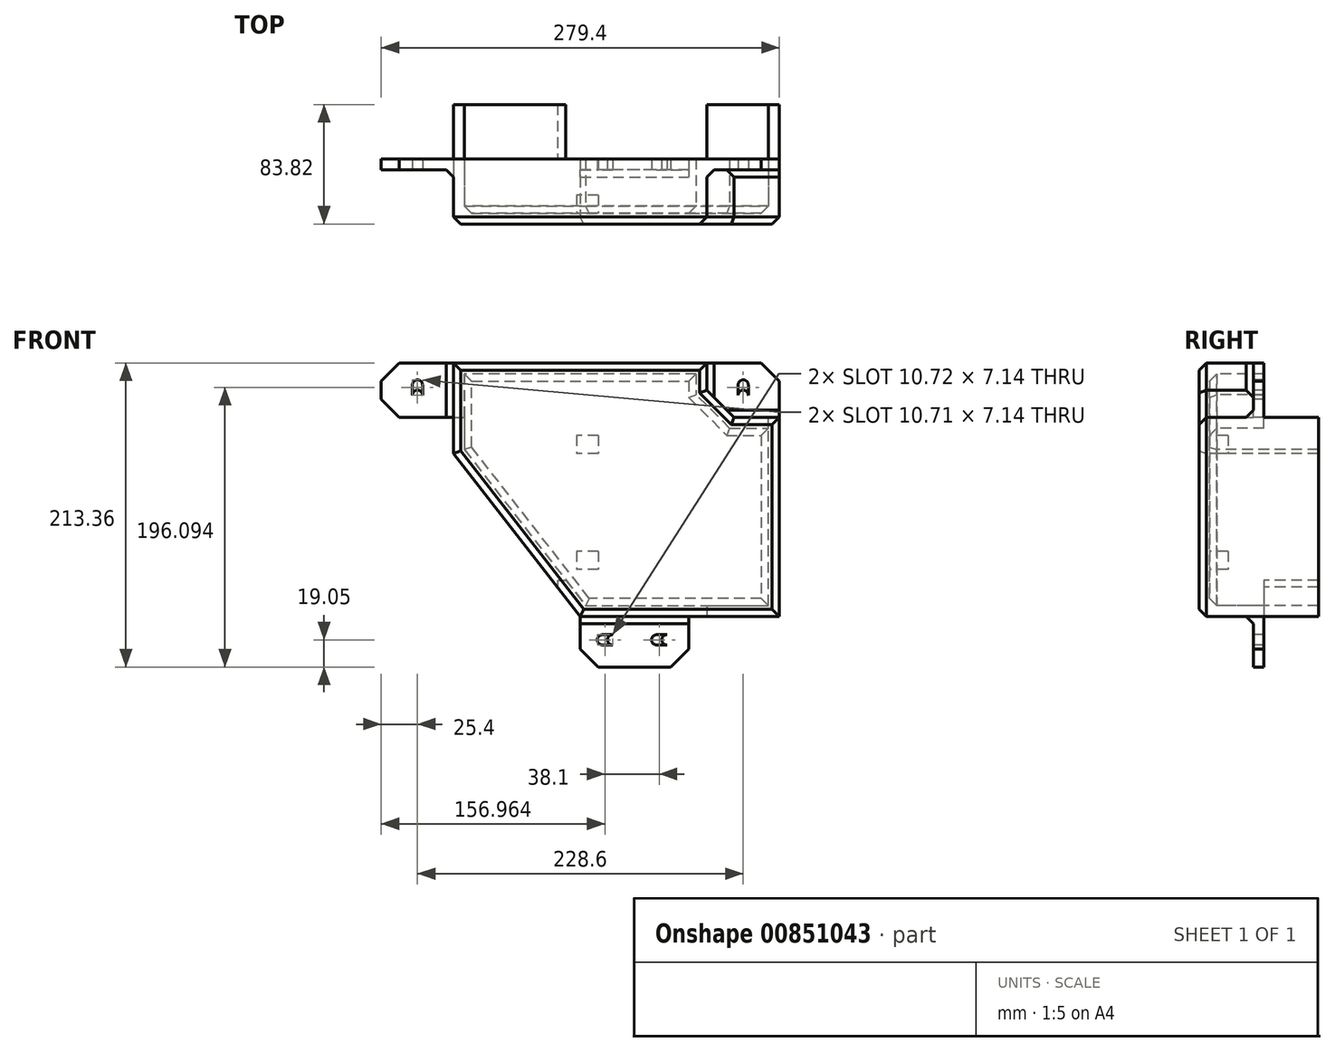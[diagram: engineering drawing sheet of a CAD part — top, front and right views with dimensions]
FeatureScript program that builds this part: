
annotation { "Feature Type Name" : "Feature", "Feature Type Description" : "" }
export const myFeature = defineFeature(function(context is Context, id is Id, definition is map)
    precondition{}
    {
        {
            var Q0;
            Q0=qCreatedBy(makeId("Front.planeOp"),FACE);
            var Q1;
            Q1=qCreatedBy(makeId("Front.planeOp"),FACE);
            var sketch = newSketch(context, id + "F0", { "sketchPlane" : qUnion([Q0, Q1])});
            skLineSegment(sketch, "E0.bottom", {"start": v(0, 0) * mm, "end": v(-279.4, 0) * mm});
            skLineSegment(sketch, "E0.top", {"start": v(0, 213.36) * mm, "end": v(-279.4, 213.36) * mm});
            skLineSegment(sketch, "E0.left", {"start": v(0, 0) * mm, "end": v(0, 213.36) * mm});
            skLineSegment(sketch, "E0.right", {"start": v(-279.4, 0) * mm, "end": v(-279.4, 213.36) * mm});
            skSolve(sketch);
        }
        {
            var Q0;
            Q0 = qSketchRegion(id + "F0", true);
            extrude(context, id + "F1", {"entities" : qUnion([Q0]), "depth" : 83.82 * mm, "offsetDistance" : 25.4 * mm});
        }
        {
            var Q0;
            Q0=makeQuery(id+"F1.opExtrude","CAP_FACE",FACE,{"disambiguationData":[OSD([sQuery(id+"F0.wireOp",EDGE,"E0.bottom"),sQuery(id+"F0.wireOp",EDGE,"E0.top"),sQuery(id+"F0.wireOp",EDGE,"E0.left"),sQuery(id+"F0.wireOp",EDGE,"E0.right")])],"isStart":false});
            var sketch = newSketch(context, id + "F2", { "sketchPlane" : qUnion([Q0])});
            skLineSegment(sketch, "E1.bottom", {"start": v(-50.8, 213.36) * mm, "end": v(0, 213.36) * mm});
            skLineSegment(sketch, "E1.top", {"start": v(-50.8, 175.26) * mm, "end": v(0, 175.26) * mm});
            skLineSegment(sketch, "E1.left", {"start": v(-50.8, 213.36) * mm, "end": v(-50.8, 175.26) * mm});
            skLineSegment(sketch, "E1.right", {"start": v(0, 213.36) * mm, "end": v(0, 175.26) * mm});
            skLineSegment(sketch, "E2", {"start": v(-228.6, 175.26) * mm, "end": v(-279.4, 175.26) * mm});
            skLineSegment(sketch, "E3", {"start": v(-228.6, 175.26) * mm, "end": v(-228.6, 213.36) * mm});
            skLineSegment(sketch, "E4", {"start": v(-228.6, 213.36) * mm, "end": v(-228.6, 149.86) * mm});
            skLineSegment(sketch, "E5", {"start": v(-228.6, 149.86) * mm, "end": v(-139.7, 35.56) * mm});
            skLineSegment(sketch, "E6", {"start": v(-139.7, 35.56) * mm, "end": v(0, 35.56) * mm});
            skLineSegment(sketch, "E7", {"start": v(-139.7, 35.56) * mm, "end": v(-139.7, 0) * mm});
            skLineSegment(sketch, "E8", {"start": v(-63.5, 35.56) * mm, "end": v(-63.5, 0) * mm});
            skLineSegment(sketch, "E9", {"start": v(-228.6, 175.26) * mm, "end": v(-50.8, 175.26) * mm});
            skLineSegment(sketch, "E10", {"start": v(-31.75, 175.26) * mm, "end": v(-50.8, 194.31) * mm});
            skSolve(sketch);
        }
        {
            var Q0;
            {var subQ1=sQuery(id+"F2.wireOp",EDGE,"E1.bottom");Q0=makeQuery(id+"F2.imprint","IMPRINT",FACE,{"disambiguationData":[TD([[makeQuery(id+"F2.imprint","IMPRINT",EDGE,{"derivedFrom":subQ1}),1.0]])]});}
            var Q1;
            {var subQ0=sQuery(id+"F2.wireOp",EDGE,"E7");Q1=makeQuery(id+"F2.imprint","IMPRINT",FACE,{"disambiguationData":[TD([[makeQuery(id+"F2.imprint","IMPRINT",EDGE,{"derivedFrom":subQ0}),1.0]])]});}
            var Q2;
            {var subQ0=sQuery(id+"F2.wireOp",EDGE,"E2");Q2=makeQuery(id+"F2.imprint","IMPRINT",FACE,{"disambiguationData":[TD([[makeQuery(id+"F2.imprint","IMPRINT",EDGE,{"derivedFrom":subQ0}),-1.0]])]});}
            var Q3;
            Q3=sQuery(id+"F2.wireOp",EDGE,"E2");
            var Q4;
            Q4=sQuery(id+"F2.wireOp",EDGE,"E3");
            var Q5;
            Q5=sQuery(id+"F2.wireOp",EDGE,"E1.left");
            var Q6;
            Q6=sQuery(id+"F2.wireOp",EDGE,"E1.top");
            var Q7;
            Q7=sQuery(id+"F2.wireOp",EDGE,"E6");
            var Q8;
            Q8=sQuery(id+"F2.wireOp",EDGE,"E7");
            extrude(context, id + "F3", {"entities" : qUnion([Q0, Q1, Q2]), "operationType" : NewBodyOperationType.REMOVE, "surfaceEntities" : qUnion([Q3, Q4, Q5, Q6, Q7, Q8]), "oppositeDirection" : true, "depth" : 38.1 * mm, "offsetDistance" : 25.4 * mm});
        }
        {
            var Q0;
            {var subQ4=sQuery(id+"F2.wireOp",EDGE,"E2");Q0=makeQuery(id+"F2.imprint","IMPRINT",FACE,{"disambiguationData":[TD([[makeQuery(id+"F2.imprint","IMPRINT",EDGE,{"derivedFrom":subQ4}),1.0]])]});}
            var Q1;
            {var subQ3=sQuery(id+"F2.wireOp",EDGE,"E8");Q1=makeQuery(id+"F2.imprint","IMPRINT",FACE,{"disambiguationData":[TD([[makeQuery(id+"F2.imprint","IMPRINT",EDGE,{"derivedFrom":subQ3}),1.0]])]});}
            extrude(context, id + "F4", {"entities" : qUnion([Q0, Q1]), "operationType" : NewBodyOperationType.REMOVE, "oppositeDirection" : true, "depth" : 83.82 * mm, "offsetDistance" : 25.4 * mm});
        }
        {
            var Q0;
            Q0=makeQuery(id+"F1.opExtrude","CAP_FACE",FACE,{"disambiguationData":[OSD([sQuery(id+"F0.wireOp",EDGE,"E0.bottom"),sQuery(id+"F0.wireOp",EDGE,"E0.top"),sQuery(id+"F0.wireOp",EDGE,"E0.left"),sQuery(id+"F0.wireOp",EDGE,"E0.right")])],"isStart":true});
            shell(context, id + "F5", {"entities" : qUnion([Q0]), "thickness" : 7.62 * mm});
        }
        {
            var Q0;
            Q0=makeQuery(id+"F1.opExtrude","SWEPT_FACE",FACE,{"disambiguationData":[OSD([sQuery(id+"F0.wireOp",EDGE,"E0.left")])]});
            var sketch = newSketch(context, id + "F6", { "sketchPlane" : qUnion([Q0])});
            skLineSegment(sketch, "E11.bottom", {"start": v(0, 213.36) * mm, "end": v(-38.1, 213.36) * mm});
            skLineSegment(sketch, "E11.top", {"start": v(0, 175.26) * mm, "end": v(-38.1, 175.26) * mm});
            skLineSegment(sketch, "E11.left", {"start": v(0, 213.36) * mm, "end": v(0, 175.26) * mm});
            skLineSegment(sketch, "E11.right", {"start": v(-38.1, 213.36) * mm, "end": v(-38.1, 175.26) * mm});
            skLineSegment(sketch, "E12.bottom", {"start": v(0, 0) * mm, "end": v(-38.1, 0) * mm});
            skLineSegment(sketch, "E12.top", {"start": v(0, 35.56) * mm, "end": v(-38.1, 35.56) * mm});
            skLineSegment(sketch, "E12.left", {"start": v(0, 0) * mm, "end": v(0, 35.56) * mm});
            skLineSegment(sketch, "E12.right", {"start": v(-38.1, 0) * mm, "end": v(-38.1, 35.56) * mm});
            skSolve(sketch);
        }
        {
            var Q0;
            Q0 = qSketchRegion(id + "F6", true);
            extrude(context, id + "F7", {"entities" : qUnion([Q0]), "operationType" : NewBodyOperationType.REMOVE, "oppositeDirection" : true, "depth" : 341.88 * mm, "offsetDistance" : 25.4 * mm});
        }
        {
            var Q0;
            Q0=makeQuery(id+"F3.boolean.opBoolean","COPY",FACE,{"derivedFrom":makeQuery(id+"F3.opExtrude","CAP_FACE",FACE,{"disambiguationData":[OSD([sQuery(id+"F0.wireOp",EDGE,"E0.bottom"),sQuery(id+"F2.wireOp",EDGE,"E6"),sQuery(id+"F2.wireOp",EDGE,"E7"),sQuery(id+"F2.wireOp",EDGE,"E8")])],"isStart":false})});
            var sketch = newSketch(context, id + "F8", { "sketchPlane" : qUnion([Q0])});
            skCircle(sketch, "E13", {"center": v(-82.55, 19.05) * mm, "radius": 3.57 * mm});
            skCircle(sketch, "E14", {"center": v(-120.65, 19.05) * mm, "radius": 3.57 * mm});
            skLineSegment(sketch, "E15", {"start": v(-139.7, 12.7) * mm, "end": v(-127, 0) * mm});
            skLineSegment(sketch, "E16", {"start": v(-76.2, 0) * mm, "end": v(-63.5, 12.7) * mm});
            skLineSegment(sketch, "E17", {"start": v(-139.7, 0) * mm, "end": v(-63.5, 0) * mm});
            skCircle(sketch, "E18", {"center": v(-254, 194.3) * mm, "radius": 3.57 * mm});
            skCircle(sketch, "E19", {"center": v(-25.4, 194.3) * mm, "radius": 3.57 * mm});
            skLineSegment(sketch, "E20.0.0", {"start": v(-228.6, 175.26) * mm, "end": v(-228.6, 213.36) * mm});
            skLineSegment(sketch, "E20.0.1", {"start": v(-228.6, 213.36) * mm, "end": v(-279.4, 213.36) * mm});
            skLineSegment(sketch, "E20.0.2", {"start": v(-279.4, 213.36) * mm, "end": v(-279.4, 175.26) * mm});
            skLineSegment(sketch, "E20.0.3", {"start": v(-279.4, 175.26) * mm, "end": v(-228.6, 175.26) * mm});
            skLineSegment(sketch, "E21.0.0", {"start": v(0, 213.36) * mm, "end": v(-50.8, 213.36) * mm});
            skLineSegment(sketch, "E21.0.1", {"start": v(-50.8, 213.36) * mm, "end": v(-50.8, 194.31) * mm});
            skLineSegment(sketch, "E21.0.3", {"start": v(0, 175.26) * mm, "end": v(0, 213.36) * mm});
            skLineSegment(sketch, "E22", {"start": v(-266.7, 175.26) * mm, "end": v(-279.4, 187.96) * mm});
            skLineSegment(sketch, "E23", {"start": v(-266.7, 213.36) * mm, "end": v(-279.4, 200.66) * mm});
            skLineSegment(sketch, "E24", {"start": v(-12.7, 213.36) * mm, "end": v(0, 200.66) * mm});
            skCircle(sketch, "E25", {"center": v(-25.4, 197.88) * mm, "radius": 3.57 * mm});
            skCircle(sketch, "E26", {"center": v(-25.4, 190.74) * mm, "radius": 3.57 * mm});
            skLineSegment(sketch, "E27", {"start": v(-21.83, 197.88) * mm, "end": v(-21.83, 190.74) * mm});
            skLineSegment(sketch, "E28", {"start": v(-28.97, 197.88) * mm, "end": v(-28.97, 190.74) * mm});
            skCircle(sketch, "E29", {"center": v(-254, 197.88) * mm, "radius": 3.57 * mm});
            skCircle(sketch, "E30", {"center": v(-254, 190.74) * mm, "radius": 3.57 * mm});
            skLineSegment(sketch, "E31", {"start": v(-257.57, 197.88) * mm, "end": v(-257.57, 190.74) * mm});
            skLineSegment(sketch, "E32", {"start": v(-250.43, 197.88) * mm, "end": v(-250.43, 190.74) * mm});
            skCircle(sketch, "E33", {"center": v(-86.12, 19.05) * mm, "radius": 3.57 * mm});
            skCircle(sketch, "E34", {"center": v(-78.98, 19.05) * mm, "radius": 3.57 * mm});
            skLineSegment(sketch, "E35", {"start": v(-86.12, 22.62) * mm, "end": v(-78.98, 22.62) * mm});
            skLineSegment(sketch, "E36", {"start": v(-78.98, 15.48) * mm, "end": v(-86.12, 15.48) * mm});
            skCircle(sketch, "E37", {"center": v(-117.08, 19.05) * mm, "radius": 3.57 * mm});
            skCircle(sketch, "E38", {"center": v(-124.22, 19.05) * mm, "radius": 3.57 * mm});
            skLineSegment(sketch, "E39", {"start": v(-124.22, 22.62) * mm, "end": v(-117.08, 22.62) * mm});
            skLineSegment(sketch, "E40", {"start": v(-117.08, 15.48) * mm, "end": v(-124.22, 15.48) * mm});
            skSolve(sketch);
        }
        {
            var Q0;
            Q0=makeQuery(id+"F8.imprint","IMPRINT",FACE,{"disambiguationData":[TD([[makeQuery(id+"F8.imprint","IMPRINT",EDGE,{"derivedFrom":sQuery(id+"F8.wireOp",EDGE,"E19")}),1.0]])]});
            var Q1;
            {var subQ3=sQuery(id+"F8.wireOp",EDGE,"E24");Q1=makeQuery(id+"F8.imprint","IMPRINT",FACE,{"disambiguationData":[TD([[makeQuery(id+"F8.imprint","IMPRINT",EDGE,{"derivedFrom":subQ3}),1.0]])]});}
            var Q2;
            Q2=makeQuery(id+"F8.imprint","IMPRINT",FACE,{"disambiguationData":[TD([[makeQuery(id+"F8.imprint","IMPRINT",EDGE,{"derivedFrom":sQuery(id+"F8.wireOp",EDGE,"E18")}),1.0]])]});
            var Q3;
            {var subQ3=sQuery(id+"F8.wireOp",EDGE,"E23");Q3=makeQuery(id+"F8.imprint","IMPRINT",FACE,{"disambiguationData":[TD([[makeQuery(id+"F8.imprint","IMPRINT",EDGE,{"derivedFrom":subQ3}),-1.0]])]});}
            var Q4;
            {var subQ3=sQuery(id+"F8.wireOp",EDGE,"E22");Q4=makeQuery(id+"F8.imprint","IMPRINT",FACE,{"disambiguationData":[TD([[makeQuery(id+"F8.imprint","IMPRINT",EDGE,{"derivedFrom":subQ3}),1.0]])]});}
            var Q5;
            {var subQ0=sQuery(id+"F8.wireOp",EDGE,"E15");Q5=makeQuery(id+"F8.imprint","IMPRINT",FACE,{"disambiguationData":[TD([[makeQuery(id+"F8.imprint","IMPRINT",EDGE,{"derivedFrom":subQ0}),-1.0]])]});}
            var Q6;
            {var subQ0=sQuery(id+"F8.wireOp",EDGE,"E16");Q6=makeQuery(id+"F8.imprint","IMPRINT",FACE,{"disambiguationData":[TD([[makeQuery(id+"F8.imprint","IMPRINT",EDGE,{"derivedFrom":subQ0}),-1.0]])]});}
            var Q7;
            Q7=makeQuery(id+"F8.imprint","IMPRINT",FACE,{"disambiguationData":[TD([[makeQuery(id+"F8.imprint","IMPRINT",EDGE,{"derivedFrom":sQuery(id+"F8.wireOp",EDGE,"E13")}),1.0]])]});
            var Q8;
            Q8=makeQuery(id+"F8.imprint","IMPRINT",FACE,{"disambiguationData":[TD([[makeQuery(id+"F8.imprint","IMPRINT",EDGE,{"derivedFrom":sQuery(id+"F8.wireOp",EDGE,"E14")}),1.0]])]});
            var Q9;
            {var subQ0=sQuery(id+"F8.wireOp",EDGE,"E25");var subQ1=sQuery(id+"F8.wireOp",EDGE,"E19");var subQ2=makeQuery(id+"F8.imprint","INTERSECT",VERTEX,{"disambiguationData":[OD(0.0)],"derivedFrom":[subQ1,subQ0]});Q9=makeQuery(id+"F8.imprint","IMPRINT",FACE,{"disambiguationData":[TD([[makeQuery(id+"F8.imprint","IMPRINT",EDGE,{"disambiguationData":[TD([[subQ2,-1.0]])],"derivedFrom":subQ1}),-1.0]])]});}
            var Q10;
            {var subQ0=sQuery(id+"F8.wireOp",EDGE,"E25");var subQ1=sQuery(id+"F8.wireOp",EDGE,"E19");var subQ2=makeQuery(id+"F8.imprint","INTERSECT",VERTEX,{"disambiguationData":[OD(0.0)],"derivedFrom":[subQ1,subQ0]});Q10=makeQuery(id+"F8.imprint","IMPRINT",FACE,{"disambiguationData":[TD([[makeQuery(id+"F8.imprint","IMPRINT",EDGE,{"disambiguationData":[TD([[subQ2,-1.0]])],"derivedFrom":subQ1}),1.0]])]});}
            var Q11;
            {var subQ0=sQuery(id+"F8.wireOp",EDGE,"E26");var subQ1=sQuery(id+"F8.wireOp",EDGE,"E19");var subQ2=makeQuery(id+"F8.imprint","INTERSECT",VERTEX,{"disambiguationData":[OD(0.0)],"derivedFrom":[subQ1,subQ0]});Q11=makeQuery(id+"F8.imprint","IMPRINT",FACE,{"disambiguationData":[TD([[makeQuery(id+"F8.imprint","IMPRINT",EDGE,{"disambiguationData":[TD([[subQ2,-1.0]])],"derivedFrom":subQ1}),1.0]])]});}
            var Q12;
            {var subQ0=sQuery(id+"F8.wireOp",EDGE,"E26");var subQ1=sQuery(id+"F8.wireOp",EDGE,"E19");var subQ2=makeQuery(id+"F8.imprint","INTERSECT",VERTEX,{"disambiguationData":[OD(0.0)],"derivedFrom":[subQ1,subQ0]});Q12=makeQuery(id+"F8.imprint","IMPRINT",FACE,{"disambiguationData":[TD([[makeQuery(id+"F8.imprint","IMPRINT",EDGE,{"disambiguationData":[TD([[subQ2,-1.0]])],"derivedFrom":subQ1}),-1.0]])]});}
            var Q13;
            {var subQ0=sQuery(id+"F8.wireOp",EDGE,"E28");var subQ1=sQuery(id+"F8.wireOp",EDGE,"E19");var subQ2=makeQuery(id+"F8.imprint","INTERSECT",VERTEX,{"derivedFrom":[subQ1,subQ0]});Q13=makeQuery(id+"F8.imprint","IMPRINT",FACE,{"disambiguationData":[TD([[makeQuery(id+"F8.imprint","IMPRINT",EDGE,{"disambiguationData":[TD([[subQ2,1.0]])],"derivedFrom":subQ1}),-1.0]])]});}
            var Q14;
            {var subQ0=sQuery(id+"F8.wireOp",EDGE,"E27");var subQ1=sQuery(id+"F8.wireOp",EDGE,"E19");var subQ2=makeQuery(id+"F8.imprint","INTERSECT",VERTEX,{"derivedFrom":[subQ1,subQ0]});Q14=makeQuery(id+"F8.imprint","IMPRINT",FACE,{"disambiguationData":[TD([[makeQuery(id+"F8.imprint","IMPRINT",EDGE,{"disambiguationData":[TD([[subQ2,-1.0]])],"derivedFrom":subQ1}),-1.0]])]});}
            var Q15;
            {var subQ0=sQuery(id+"F8.wireOp",EDGE,"E27");var subQ1=sQuery(id+"F8.wireOp",EDGE,"E19");var subQ2=makeQuery(id+"F8.imprint","INTERSECT",VERTEX,{"derivedFrom":[subQ1,subQ0]});Q15=makeQuery(id+"F8.imprint","IMPRINT",FACE,{"disambiguationData":[TD([[makeQuery(id+"F8.imprint","IMPRINT",EDGE,{"disambiguationData":[TD([[subQ2,1.0]])],"derivedFrom":subQ1}),-1.0]])]});}
            var Q16;
            {var subQ0=sQuery(id+"F8.wireOp",EDGE,"E28");var subQ1=sQuery(id+"F8.wireOp",EDGE,"E19");var subQ2=makeQuery(id+"F8.imprint","INTERSECT",VERTEX,{"derivedFrom":[subQ1,subQ0]});Q16=makeQuery(id+"F8.imprint","IMPRINT",FACE,{"disambiguationData":[TD([[makeQuery(id+"F8.imprint","IMPRINT",EDGE,{"disambiguationData":[TD([[subQ2,-1.0]])],"derivedFrom":subQ1}),-1.0]])]});}
            var Q17;
            {var subQ0=sQuery(id+"F8.wireOp",EDGE,"E38");var subQ1=sQuery(id+"F8.wireOp",EDGE,"E14");var subQ2=makeQuery(id+"F8.imprint","INTERSECT",VERTEX,{"disambiguationData":[OD(0.0)],"derivedFrom":[subQ1,subQ0]});Q17=makeQuery(id+"F8.imprint","IMPRINT",FACE,{"disambiguationData":[TD([[makeQuery(id+"F8.imprint","IMPRINT",EDGE,{"disambiguationData":[TD([[subQ2,-1.0]])],"derivedFrom":subQ1}),1.0]])]});}
            var Q18;
            {var subQ0=sQuery(id+"F8.wireOp",EDGE,"E37");var subQ1=sQuery(id+"F8.wireOp",EDGE,"E14");var subQ2=makeQuery(id+"F8.imprint","INTERSECT",VERTEX,{"disambiguationData":[OD(0.0)],"derivedFrom":[subQ1,subQ0]});Q18=makeQuery(id+"F8.imprint","IMPRINT",FACE,{"disambiguationData":[TD([[makeQuery(id+"F8.imprint","IMPRINT",EDGE,{"disambiguationData":[TD([[subQ2,1.0]])],"derivedFrom":subQ1}),1.0]])]});}
            var Q19;
            {var subQ0=sQuery(id+"F8.wireOp",EDGE,"E37");var subQ1=sQuery(id+"F8.wireOp",EDGE,"E14");var subQ2=makeQuery(id+"F8.imprint","INTERSECT",VERTEX,{"disambiguationData":[OD(0.0)],"derivedFrom":[subQ1,subQ0]});Q19=makeQuery(id+"F8.imprint","IMPRINT",FACE,{"disambiguationData":[TD([[makeQuery(id+"F8.imprint","IMPRINT",EDGE,{"disambiguationData":[TD([[subQ2,1.0]])],"derivedFrom":subQ1}),-1.0]])]});}
            var Q20;
            {var subQ0=sQuery(id+"F8.wireOp",EDGE,"E38");var subQ1=sQuery(id+"F8.wireOp",EDGE,"E14");var subQ2=makeQuery(id+"F8.imprint","INTERSECT",VERTEX,{"disambiguationData":[OD(0.0)],"derivedFrom":[subQ1,subQ0]});Q20=makeQuery(id+"F8.imprint","IMPRINT",FACE,{"disambiguationData":[TD([[makeQuery(id+"F8.imprint","IMPRINT",EDGE,{"disambiguationData":[TD([[subQ2,-1.0]])],"derivedFrom":subQ1}),-1.0]])]});}
            var Q21;
            {var subQ0=sQuery(id+"F8.wireOp",EDGE,"E39");var subQ1=sQuery(id+"F8.wireOp",EDGE,"E14");var subQ2=makeQuery(id+"F8.imprint","INTERSECT",VERTEX,{"derivedFrom":[subQ1,subQ0]});Q21=makeQuery(id+"F8.imprint","IMPRINT",FACE,{"disambiguationData":[TD([[makeQuery(id+"F8.imprint","IMPRINT",EDGE,{"disambiguationData":[TD([[subQ2,1.0]])],"derivedFrom":subQ1}),-1.0]])]});}
            var Q22;
            {var subQ0=sQuery(id+"F8.wireOp",EDGE,"E39");var subQ1=sQuery(id+"F8.wireOp",EDGE,"E14");var subQ2=makeQuery(id+"F8.imprint","INTERSECT",VERTEX,{"derivedFrom":[subQ1,subQ0]});Q22=makeQuery(id+"F8.imprint","IMPRINT",FACE,{"disambiguationData":[TD([[makeQuery(id+"F8.imprint","IMPRINT",EDGE,{"disambiguationData":[TD([[subQ2,-1.0]])],"derivedFrom":subQ1}),-1.0]])]});}
            var Q23;
            {var subQ0=sQuery(id+"F8.wireOp",EDGE,"E40");var subQ1=sQuery(id+"F8.wireOp",EDGE,"E14");var subQ2=makeQuery(id+"F8.imprint","INTERSECT",VERTEX,{"derivedFrom":[subQ1,subQ0]});Q23=makeQuery(id+"F8.imprint","IMPRINT",FACE,{"disambiguationData":[TD([[makeQuery(id+"F8.imprint","IMPRINT",EDGE,{"disambiguationData":[TD([[subQ2,-1.0]])],"derivedFrom":subQ1}),-1.0]])]});}
            var Q24;
            {var subQ0=sQuery(id+"F8.wireOp",EDGE,"E38");var subQ1=sQuery(id+"F8.wireOp",EDGE,"E14");var subQ2=makeQuery(id+"F8.imprint","INTERSECT",VERTEX,{"disambiguationData":[OD(1.0)],"derivedFrom":[subQ1,subQ0]});Q24=makeQuery(id+"F8.imprint","IMPRINT",FACE,{"disambiguationData":[TD([[makeQuery(id+"F8.imprint","IMPRINT",EDGE,{"disambiguationData":[TD([[subQ2,-1.0]])],"derivedFrom":subQ1}),-1.0]])]});}
            var Q25;
            {var subQ0=sQuery(id+"F8.wireOp",EDGE,"E35");var subQ1=sQuery(id+"F8.wireOp",EDGE,"E13");var subQ2=makeQuery(id+"F8.imprint","INTERSECT",VERTEX,{"derivedFrom":[subQ1,subQ0]});Q25=makeQuery(id+"F8.imprint","IMPRINT",FACE,{"disambiguationData":[TD([[makeQuery(id+"F8.imprint","IMPRINT",EDGE,{"disambiguationData":[TD([[subQ2,1.0]])],"derivedFrom":subQ1}),-1.0]])]});}
            var Q26;
            {var subQ0=sQuery(id+"F8.wireOp",EDGE,"E35");var subQ1=sQuery(id+"F8.wireOp",EDGE,"E13");var subQ2=makeQuery(id+"F8.imprint","INTERSECT",VERTEX,{"derivedFrom":[subQ1,subQ0]});Q26=makeQuery(id+"F8.imprint","IMPRINT",FACE,{"disambiguationData":[TD([[makeQuery(id+"F8.imprint","IMPRINT",EDGE,{"disambiguationData":[TD([[subQ2,-1.0]])],"derivedFrom":subQ1}),-1.0]])]});}
            var Q27;
            {var subQ0=sQuery(id+"F8.wireOp",EDGE,"E33");var subQ1=sQuery(id+"F8.wireOp",EDGE,"E13");var subQ2=makeQuery(id+"F8.imprint","INTERSECT",VERTEX,{"disambiguationData":[OD(0.0)],"derivedFrom":[subQ1,subQ0]});Q27=makeQuery(id+"F8.imprint","IMPRINT",FACE,{"disambiguationData":[TD([[makeQuery(id+"F8.imprint","IMPRINT",EDGE,{"disambiguationData":[TD([[subQ2,-1.0]])],"derivedFrom":subQ1}),-1.0]])]});}
            var Q28;
            {var subQ0=sQuery(id+"F8.wireOp",EDGE,"E33");var subQ1=sQuery(id+"F8.wireOp",EDGE,"E13");var subQ2=makeQuery(id+"F8.imprint","INTERSECT",VERTEX,{"disambiguationData":[OD(0.0)],"derivedFrom":[subQ1,subQ0]});Q28=makeQuery(id+"F8.imprint","IMPRINT",FACE,{"disambiguationData":[TD([[makeQuery(id+"F8.imprint","IMPRINT",EDGE,{"disambiguationData":[TD([[subQ2,-1.0]])],"derivedFrom":subQ1}),1.0]])]});}
            var Q29;
            {var subQ0=sQuery(id+"F8.wireOp",EDGE,"E34");var subQ1=sQuery(id+"F8.wireOp",EDGE,"E13");var subQ2=makeQuery(id+"F8.imprint","INTERSECT",VERTEX,{"disambiguationData":[OD(0.0)],"derivedFrom":[subQ1,subQ0]});Q29=makeQuery(id+"F8.imprint","IMPRINT",FACE,{"disambiguationData":[TD([[makeQuery(id+"F8.imprint","IMPRINT",EDGE,{"disambiguationData":[TD([[subQ2,1.0]])],"derivedFrom":subQ1}),1.0]])]});}
            var Q30;
            {var subQ0=sQuery(id+"F8.wireOp",EDGE,"E34");var subQ1=sQuery(id+"F8.wireOp",EDGE,"E13");var subQ2=makeQuery(id+"F8.imprint","INTERSECT",VERTEX,{"disambiguationData":[OD(0.0)],"derivedFrom":[subQ1,subQ0]});Q30=makeQuery(id+"F8.imprint","IMPRINT",FACE,{"disambiguationData":[TD([[makeQuery(id+"F8.imprint","IMPRINT",EDGE,{"disambiguationData":[TD([[subQ2,1.0]])],"derivedFrom":subQ1}),-1.0]])]});}
            var Q31;
            {var subQ0=sQuery(id+"F8.wireOp",EDGE,"E36");var subQ1=sQuery(id+"F8.wireOp",EDGE,"E13");var subQ2=makeQuery(id+"F8.imprint","INTERSECT",VERTEX,{"derivedFrom":[subQ1,subQ0]});Q31=makeQuery(id+"F8.imprint","IMPRINT",FACE,{"disambiguationData":[TD([[makeQuery(id+"F8.imprint","IMPRINT",EDGE,{"disambiguationData":[TD([[subQ2,-1.0]])],"derivedFrom":subQ1}),-1.0]])]});}
            var Q32;
            {var subQ0=sQuery(id+"F8.wireOp",EDGE,"E33");var subQ1=sQuery(id+"F8.wireOp",EDGE,"E13");var subQ2=makeQuery(id+"F8.imprint","INTERSECT",VERTEX,{"disambiguationData":[OD(1.0)],"derivedFrom":[subQ1,subQ0]});Q32=makeQuery(id+"F8.imprint","IMPRINT",FACE,{"disambiguationData":[TD([[makeQuery(id+"F8.imprint","IMPRINT",EDGE,{"disambiguationData":[TD([[subQ2,-1.0]])],"derivedFrom":subQ1}),-1.0]])]});}
            var Q33;
            {var subQ0=sQuery(id+"F8.wireOp",EDGE,"E29");var subQ1=sQuery(id+"F8.wireOp",EDGE,"E18");var subQ2=makeQuery(id+"F8.imprint","INTERSECT",VERTEX,{"disambiguationData":[OD(0.0)],"derivedFrom":[subQ1,subQ0]});Q33=makeQuery(id+"F8.imprint","IMPRINT",FACE,{"disambiguationData":[TD([[makeQuery(id+"F8.imprint","IMPRINT",EDGE,{"disambiguationData":[TD([[subQ2,-1.0]])],"derivedFrom":subQ1}),1.0]])]});}
            var Q34;
            {var subQ0=sQuery(id+"F8.wireOp",EDGE,"E29");var subQ1=sQuery(id+"F8.wireOp",EDGE,"E18");var subQ2=makeQuery(id+"F8.imprint","INTERSECT",VERTEX,{"disambiguationData":[OD(0.0)],"derivedFrom":[subQ1,subQ0]});Q34=makeQuery(id+"F8.imprint","IMPRINT",FACE,{"disambiguationData":[TD([[makeQuery(id+"F8.imprint","IMPRINT",EDGE,{"disambiguationData":[TD([[subQ2,-1.0]])],"derivedFrom":subQ1}),-1.0]])]});}
            var Q35;
            {var subQ0=sQuery(id+"F8.wireOp",EDGE,"E30");var subQ1=sQuery(id+"F8.wireOp",EDGE,"E18");var subQ2=makeQuery(id+"F8.imprint","INTERSECT",VERTEX,{"disambiguationData":[OD(0.0)],"derivedFrom":[subQ1,subQ0]});Q35=makeQuery(id+"F8.imprint","IMPRINT",FACE,{"disambiguationData":[TD([[makeQuery(id+"F8.imprint","IMPRINT",EDGE,{"disambiguationData":[TD([[subQ2,-1.0]])],"derivedFrom":subQ1}),1.0]])]});}
            var Q36;
            {var subQ0=sQuery(id+"F8.wireOp",EDGE,"E30");var subQ1=sQuery(id+"F8.wireOp",EDGE,"E18");var subQ2=makeQuery(id+"F8.imprint","INTERSECT",VERTEX,{"disambiguationData":[OD(0.0)],"derivedFrom":[subQ1,subQ0]});Q36=makeQuery(id+"F8.imprint","IMPRINT",FACE,{"disambiguationData":[TD([[makeQuery(id+"F8.imprint","IMPRINT",EDGE,{"disambiguationData":[TD([[subQ2,-1.0]])],"derivedFrom":subQ1}),-1.0]])]});}
            var Q37;
            {var subQ0=sQuery(id+"F8.wireOp",EDGE,"E32");var subQ1=sQuery(id+"F8.wireOp",EDGE,"E18");var subQ2=makeQuery(id+"F8.imprint","INTERSECT",VERTEX,{"derivedFrom":[subQ1,subQ0]});Q37=makeQuery(id+"F8.imprint","IMPRINT",FACE,{"disambiguationData":[TD([[makeQuery(id+"F8.imprint","IMPRINT",EDGE,{"disambiguationData":[TD([[subQ2,1.0]])],"derivedFrom":subQ1}),-1.0]])]});}
            var Q38;
            {var subQ0=sQuery(id+"F8.wireOp",EDGE,"E29");var subQ1=sQuery(id+"F8.wireOp",EDGE,"E18");var subQ2=makeQuery(id+"F8.imprint","INTERSECT",VERTEX,{"disambiguationData":[OD(0.0)],"derivedFrom":[subQ1,subQ0]});Q38=makeQuery(id+"F8.imprint","IMPRINT",FACE,{"disambiguationData":[TD([[makeQuery(id+"F8.imprint","IMPRINT",EDGE,{"disambiguationData":[TD([[subQ2,1.0]])],"derivedFrom":subQ1}),-1.0]])]});}
            var Q39;
            {var subQ0=sQuery(id+"F8.wireOp",EDGE,"E29");var subQ1=sQuery(id+"F8.wireOp",EDGE,"E18");var subQ2=makeQuery(id+"F8.imprint","INTERSECT",VERTEX,{"disambiguationData":[OD(1.0)],"derivedFrom":[subQ1,subQ0]});Q39=makeQuery(id+"F8.imprint","IMPRINT",FACE,{"disambiguationData":[TD([[makeQuery(id+"F8.imprint","IMPRINT",EDGE,{"disambiguationData":[TD([[subQ2,-1.0]])],"derivedFrom":subQ1}),-1.0]])]});}
            var Q40;
            {var subQ0=sQuery(id+"F8.wireOp",EDGE,"E31");var subQ1=sQuery(id+"F8.wireOp",EDGE,"E18");var subQ2=makeQuery(id+"F8.imprint","INTERSECT",VERTEX,{"derivedFrom":[subQ1,subQ0]});Q40=makeQuery(id+"F8.imprint","IMPRINT",FACE,{"disambiguationData":[TD([[makeQuery(id+"F8.imprint","IMPRINT",EDGE,{"disambiguationData":[TD([[subQ2,-1.0]])],"derivedFrom":subQ1}),-1.0]])]});}
            extrude(context, id + "F9", {"entities" : qUnion([Q0, Q1, Q2, Q3, Q4, Q5, Q6, Q7, Q8, Q9, Q10, Q11, Q12, Q13, Q14, Q15, Q16, Q17, Q18, Q19, Q20, Q21, Q22, Q23, Q24, Q25, Q26, Q27, Q28, Q29, Q30, Q31, Q32, Q33, Q34, Q35, Q36, Q37, Q38, Q39, Q40]), "operationType" : NewBodyOperationType.REMOVE, "oppositeDirection" : true, "depth" : 7.62 * mm, "offsetDistance" : 25.4 * mm});
        }
        {
            var Q0;
            Q0=makeQuery(id+"F3.boolean.opBoolean","COPY",EDGE,{"derivedFrom":makeQuery(id+"F3.opExtrude","CAP_EDGE",EDGE,{"disambiguationData":[OSD([sQuery(id+"F2.wireOp",EDGE,"E1.left")])],"isStart":false})});
            var Q1;
            Q1=makeQuery(id+"F3.boolean.opBoolean","COPY",EDGE,{"derivedFrom":makeQuery(id+"F3.opExtrude","CAP_EDGE",EDGE,{"disambiguationData":[OSD([sQuery(id+"F2.wireOp",EDGE,"E1.top")])],"isStart":false})});
            var Q2;
            Q2=makeQuery(id+"F3.boolean.opBoolean","COPY",EDGE,{"derivedFrom":makeQuery(id+"F3.opExtrude","CAP_EDGE",EDGE,{"disambiguationData":[OSD([sQuery(id+"F2.wireOp",EDGE,"E3")])],"isStart":false})});
            var Q3;
            Q3=makeQuery(id+"F3.boolean.opBoolean","COPY",EDGE,{"derivedFrom":makeQuery(id+"F3.opExtrude","CAP_EDGE",EDGE,{"disambiguationData":[OSD([sQuery(id+"F2.wireOp",EDGE,"E6")])],"isStart":false})});
            var Q4;
            Q4=makeQuery(id+"F5.opShell","OFFSET_FACE",FACE,{"disambiguationData":[OSD([sQuery(id+"F0.wireOp",EDGE,"E0.bottom"),sQuery(id+"F0.wireOp",EDGE,"E0.top"),sQuery(id+"F0.wireOp",EDGE,"E0.left"),sQuery(id+"F0.wireOp",EDGE,"E0.right")])]});
            var Q5;
            Q5=makeQuery(id+"F1.opExtrude","CAP_FACE",FACE,{"disambiguationData":[OSD([sQuery(id+"F0.wireOp",EDGE,"E0.bottom"),sQuery(id+"F0.wireOp",EDGE,"E0.top"),sQuery(id+"F0.wireOp",EDGE,"E0.left"),sQuery(id+"F0.wireOp",EDGE,"E0.right")])],"isStart":false});
            chamfer(context, id + "F10", {"entities" : qUnion([Q0, Q1, Q2, Q3, Q4, Q5]), "width" : 5.08 * mm, "tangentPropagation" : true});
        }
        {
            var Q0;
            {var subQ0=sQuery(id+"F2.wireOp",EDGE,"E6");Q0=makeQuery(id+"F7.boolean.opBoolean","MERGE",FACE,{"derivedFrom":[makeQuery(id+"F4.boolean.opBoolean","MERGE",FACE,{"derivedFrom":[makeQuery(id+"F3.boolean.opBoolean","COPY",FACE,{"derivedFrom":makeQuery(id+"F3.opExtrude","SWEPT_FACE",FACE,{"disambiguationData":[OSD([subQ0])]})})],"fromTools":[makeQuery(id+"F4.opExtrude","SWEPT_FACE",FACE,{"disambiguationData":[OSD([subQ0])]})]})],"fromTools":[makeQuery(id+"F7.opExtrude","SWEPT_FACE",FACE,{"disambiguationData":[OSD([sQuery(id+"F6.wireOp",EDGE,"E12.top")])]})]});}
            var sketch = newSketch(context, id + "F11", { "sketchPlane" : qUnion([Q0])});
            skLineSegment(sketch, "E41.bottom", {"start": v(-155.58, 0) * mm, "end": v(-50.8, 0) * mm});
            skLineSegment(sketch, "E41.top", {"start": v(-155.58, 38.1) * mm, "end": v(-50.8, 38.1) * mm});
            skLineSegment(sketch, "E41.left", {"start": v(-155.58, 0) * mm, "end": v(-155.58, 38.1) * mm});
            skLineSegment(sketch, "E41.right", {"start": v(-50.8, 0) * mm, "end": v(-50.8, 38.1) * mm});
            skSolve(sketch);
        }
        {
            var Q0;
            {var subQ6=sQuery(id+"F11.wireOp",EDGE,"E41.right");Q0=makeQuery(id+"F11.imprint","IMPRINT",FACE,{"disambiguationData":[TD([[makeQuery(id+"F11.imprint","IMPRINT",EDGE,{"derivedFrom":subQ6}),1.0]])]});}
            var Q1;
            {var subQ2=sQuery(id+"F11.wireOp",EDGE,"E41.left");Q1=makeQuery(id+"F11.imprint","IMPRINT",FACE,{"disambiguationData":[TD([[makeQuery(id+"F11.imprint","IMPRINT",EDGE,{"derivedFrom":subQ2}),-1.0]])]});}
            extrude(context, id + "F12", {"entities" : qUnion([Q0, Q1]), "operationType" : NewBodyOperationType.REMOVE, "oppositeDirection" : true, "depth" : 25.4 * mm, "offsetDistance" : 25.4 * mm});
        }
        {
            var Q0;
            Q0=makeQuery(id+"F5.opShell","OFFSET_FACE",FACE,{"disambiguationData":[OSD([sQuery(id+"F0.wireOp",EDGE,"E0.bottom"),sQuery(id+"F0.wireOp",EDGE,"E0.top"),sQuery(id+"F0.wireOp",EDGE,"E0.left"),sQuery(id+"F0.wireOp",EDGE,"E0.right")])]});
            var sketch = newSketch(context, id + "F13", { "sketchPlane" : qUnion([Q0])});
            skLineSegment(sketch, "E42.bottom", {"start": v(127, 162.56) * mm, "end": v(142.24, 162.56) * mm});
            skLineSegment(sketch, "E42.top", {"start": v(127, 149.86) * mm, "end": v(142.24, 149.86) * mm});
            skLineSegment(sketch, "E42.left", {"start": v(127, 162.56) * mm, "end": v(127, 149.86) * mm});
            skLineSegment(sketch, "E42.right", {"start": v(142.24, 162.56) * mm, "end": v(142.24, 149.86) * mm});
            skLineSegment(sketch, "E43.bottom", {"start": v(127, 81.28) * mm, "end": v(142.24, 81.28) * mm});
            skLineSegment(sketch, "E43.top", {"start": v(127, 68.58) * mm, "end": v(142.24, 68.58) * mm});
            skLineSegment(sketch, "E43.left", {"start": v(127, 81.28) * mm, "end": v(127, 68.58) * mm});
            skLineSegment(sketch, "E43.right", {"start": v(142.24, 81.28) * mm, "end": v(142.24, 68.58) * mm});
            skSolve(sketch);
        }
        {
            var Q0;
            Q0=makeQuery(id+"F13.imprint","IMPRINT",FACE,{"disambiguationData":[TD([[makeQuery(id+"F13.imprint","IMPRINT",EDGE,{"derivedFrom":sQuery(id+"F13.wireOp",EDGE,"sCbw7942-BY85-1mlW-8CTV-JDFPvkmrLgGv.bottom")}),-1.0]])]});
            var Q1;
            Q1=makeQuery(id+"F13.imprint","IMPRINT",FACE,{"disambiguationData":[TD([[makeQuery(id+"F13.imprint","IMPRINT",EDGE,{"derivedFrom":sQuery(id+"F13.wireOp",EDGE,"E42.bottom")}),-1.0]])]});
            var Q2;
            Q2=makeQuery(id+"F13.imprint","IMPRINT",FACE,{"disambiguationData":[TD([[makeQuery(id+"F13.imprint","IMPRINT",EDGE,{"derivedFrom":sQuery(id+"F13.wireOp",EDGE,"E43.bottom")}),-1.0]])]});
            extrude(context, id + "F14", {"entities" : qUnion([Q0, Q1, Q2]), "operationType" : NewBodyOperationType.ADD, "depth" : 12.7 * mm, "offsetDistance" : 25.4 * mm});
        }
    });
